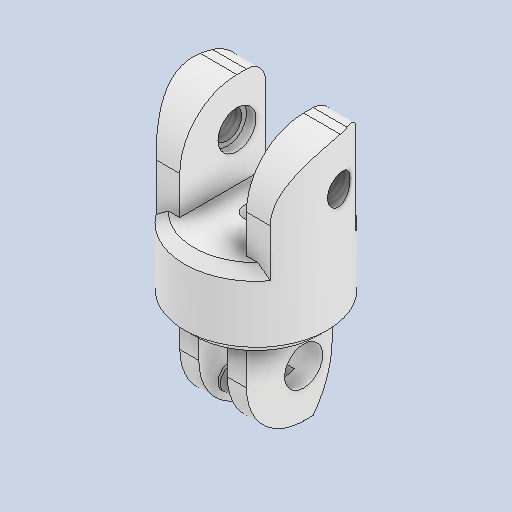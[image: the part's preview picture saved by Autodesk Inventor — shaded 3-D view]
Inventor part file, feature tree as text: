
AUTODESK INVENTOR PART (.ipt)
format: ipt  version: 2022 (Build 260153000, 153)  size: 264,704 bytes
history: native  units: in
note: dims shown in document units (in); Inventor stores cm internally (conversion verified against a paired STEP export)
features: sketch x10, extrude x7, fillet x5, chamfer x4, hole x3, thread x2
ambient origin geometry x8: Origin, YZ Plane, XZ Plane, XY Plane, X Axis, Y Axis, Z Axis, Center Point
bodies: Solid1 (feature_tree)
feature tree (31):
  extrude  "Extrusion1"  Depth=0.3937in
  fillet  "Fillet1"  Radius=0.3937in
  fillet  "Fillet2"  Radius=0.5906in
  extrude  "Extrusion2"  Depth=0.0787in TaperAngle=0.0deg
  chamfer  "Chamfer1"  Distance=0.0787in Angle=45.0deg
  fillet  "Fillet3"  Radius=0.0098in
  hole  "Hole1"  [1 undecoded]
  extrude  "Extrusion3"  Depth=0.0591in TaperAngle=0.0deg
  chamfer  "Chamfer2"  Distance=0.0098in Angle=45.0deg
  extrude  "Extrusion4"  Depth=0.3937in TaperAngle=0.0deg
  chamfer  "Chamfer3"  Distance=0.3937in
  extrude  "Extrusion5"  Depth=0.2362in
  extrude  "Extrusion6"  Depth=0.0787in
  chamfer  "Chamfer5"  Distance=0.2362in
  fillet  "Fillet4"  Radius=0.2362in
  fillet  "Fillet5"  Radius=0.0197in
  hole  "Hole2"  [1 undecoded]
  hole  "Hole3"  [1 undecoded]
  thread  "Thread1"  [1 undecoded]
  thread  "Thread2"  [1 undecoded]
  sketch  "Sketch1"  dims[d8=0.3937in d9=0.0in d10=0.2362in d11=0.3937in d12=0.5906in]
  sketch  "Sketch2"  dims[d13=0.0984in d14=0.0394in d15=0.0in d16=0.0394in d17=0.0787in d18=45.0deg d19=0.0098in]
  sketch  "Sketch3"  dims[d20=0.1969in]
  sketch  "Sketch4"  dims[d21=0.1575in d22=0.2362in d23=0.1575in d24=0.0787in d25=90.0deg d26=0.3937in d27=0.0in d31=0.0591in d32=0.0in]
  sketch  "Sketch5"  dims[d33=0.0098in d34=0.0492in d35=45.0deg d36=0.0591in d37=0.0in d38=0.0098in d39=0.0492in d40=45.0deg]
  sketch  "Sketch6"  dims[d41=0.2362in d42=0.0in d43=0.0394in d44=0.0in d56=0.0in d57=0.3937in]
  sketch  "Sketch7"  dims[d58=0.0394in d59=0.0492in d60=45.0deg d61=0.2362in]
  sketch  "Sketch11"  dims[d64=0.1181in d65=0.2362in d66=0.1575in d67=0.0394in d68=90.0deg d69=0.1575in d70=0.0in]
  sketch  "Sketch12"  dims[d71=0.1969in d72=0.1181in d73=0.2362in d74=0.1575in d75=0.0394in d76=90.0deg d77=0.1575in d78=0.0in d79=0.2362in d80=0.0in d81=0.2362in d82=0.0in d52=0.0197in d53=0.0344in d54=0.0197in d55=0.0344in]
  extrude  "Extrusion9"  [1 undecoded]
  sketch  "Sketch10"  dims[d62=0.0787in d63=0.1969in]
note: 6 required parameter values undecoded (feature->parameter linkage not recoverable at this tier; creation-order binding heuristic only, values carry confidence <= 0.55)
